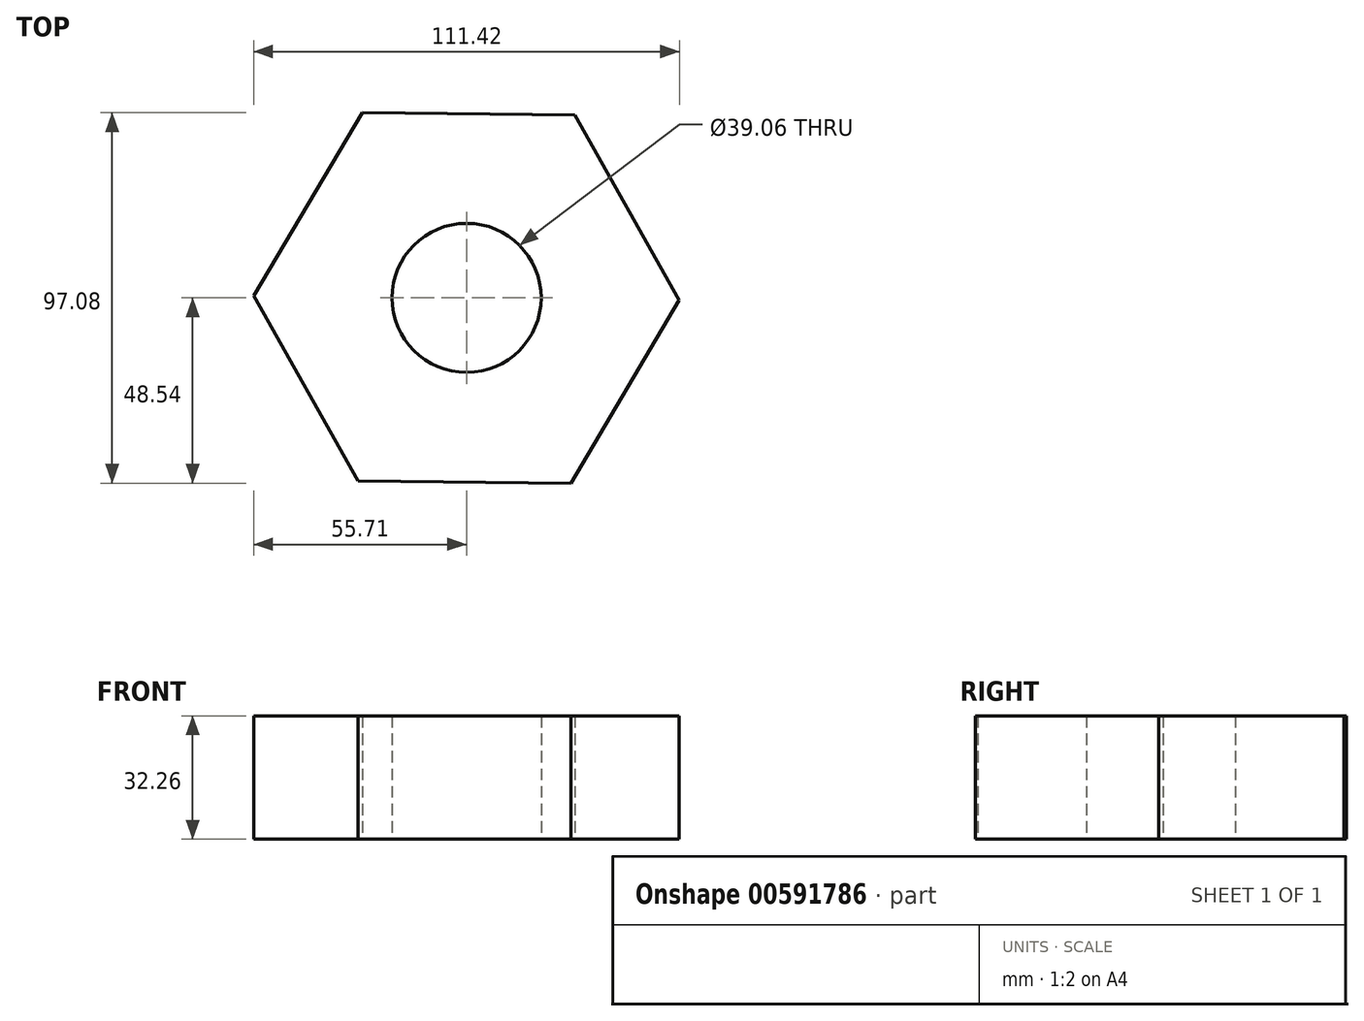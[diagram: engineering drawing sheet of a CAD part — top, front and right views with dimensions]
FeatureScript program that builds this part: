
annotation { "Feature Type Name" : "Feature", "Feature Type Description" : "" }
export const myFeature = defineFeature(function(context is Context, id is Id, definition is map)
    precondition{}
    {
        {
            var Q0;
            Q0=qCreatedBy(makeId("Top.planeOp"),FACE);
            var sketch = newSketch(context, id + "F0", { "sketchPlane" : qUnion([Q0])});
            skCircle(sketch, "E0.cCircle", {"center": v(0, 0) * mm, "radius": 48.25 * mm, "construction": true});
            skLineSegment(sketch, "E0.0", {"start": v(55.7, -0.6) * mm, "end": v(27.34, -48.54) * mm});
            skLineSegment(sketch, "E0.1", {"start": v(27.34, -48.54) * mm, "end": v(-28.37, -47.95) * mm});
            skLineSegment(sketch, "E0.2", {"start": v(-28.37, -47.95) * mm, "end": v(-55.7, 0.6) * mm});
            skLineSegment(sketch, "E0.3", {"start": v(-55.7, 0.6) * mm, "end": v(-27.34, 48.54) * mm});
            skLineSegment(sketch, "E0.4", {"start": v(-27.34, 48.54) * mm, "end": v(28.37, 47.95) * mm});
            skLineSegment(sketch, "E0.5", {"start": v(28.37, 47.95) * mm, "end": v(55.7, -0.6) * mm});
            skPoint(sketch, "E0.0.midPoint", {"position": v(41.52, -24.57) * mm});
            skCircle(sketch, "E1", {"center": v(0, 0) * mm, "radius": 19.53 * mm});
            skSolve(sketch);
        }
        {
            var Q0;
            Q0 = qSketchRegion(id + "F0", true);
            extrude(context, id + "F1", {"entities" : qUnion([Q0]), "depth" : 32.26 * mm, "offsetDistance" : 25.4 * mm});
        }
    });
